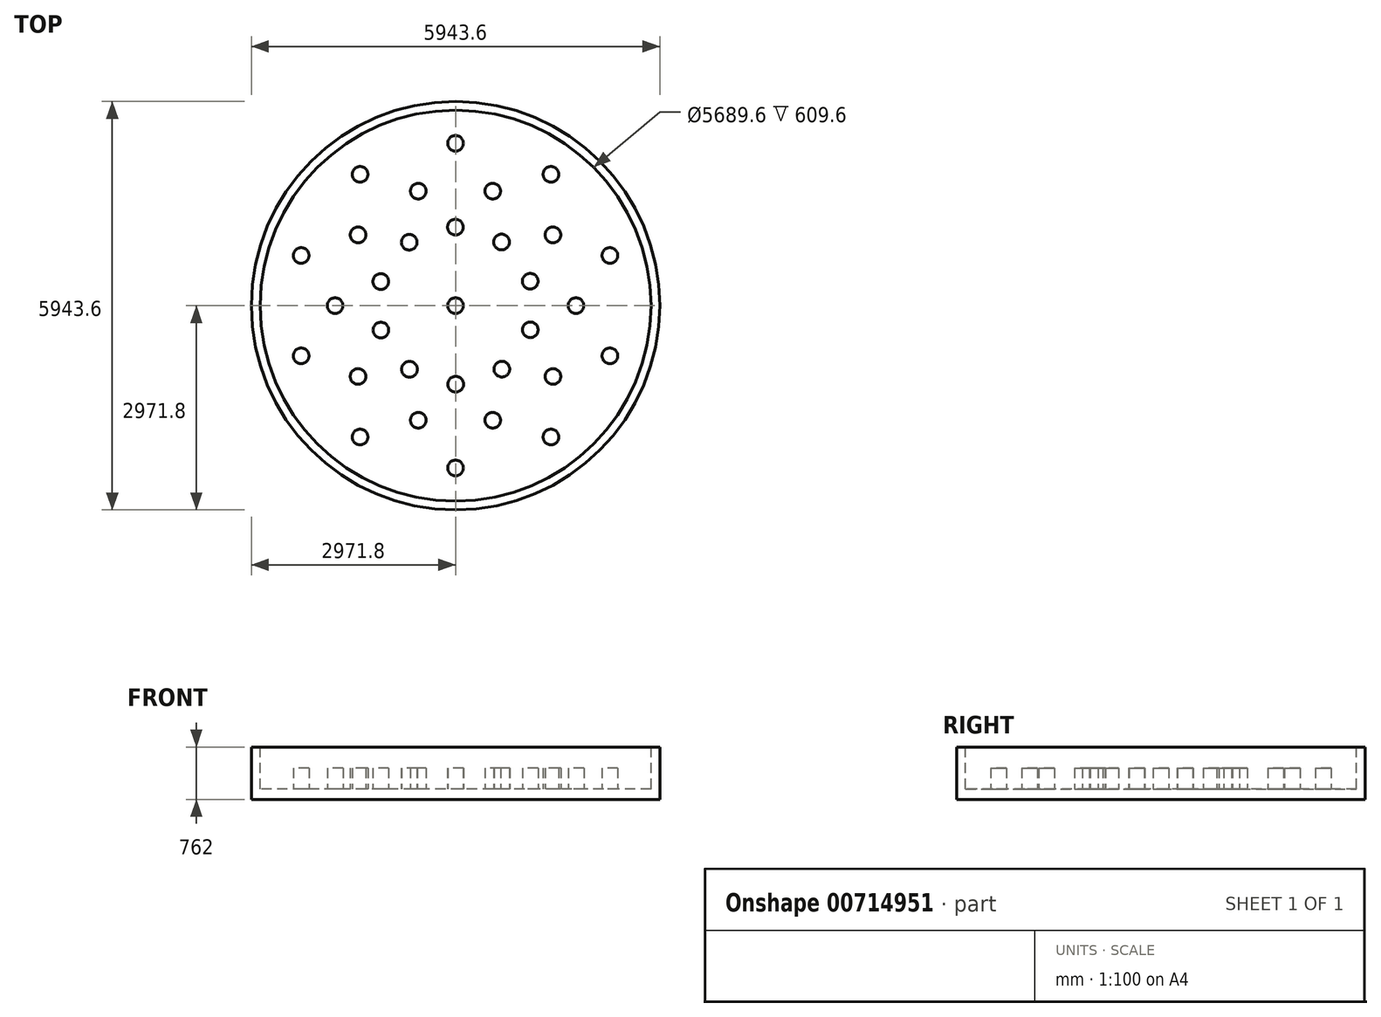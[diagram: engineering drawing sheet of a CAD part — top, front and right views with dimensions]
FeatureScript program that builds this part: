
annotation { "Feature Type Name" : "Feature", "Feature Type Description" : "" }
export const myFeature = defineFeature(function(context is Context, id is Id, definition is map)
    precondition{}
    {
        {
            var Q0;
            Q0=qCreatedBy(makeId("Top.planeOp"),FACE);
            var sketch = newSketch(context, id + "F0", { "sketchPlane" : qUnion([Q0])});
            skCircle(sketch, "E0", {"center": v(0, 0) * mm, "radius": 2971.8 * mm});
            skSolve(sketch);
        }
        {
            var Q0;
            Q0=makeQuery(id+"F0.imprint","IMPRINT",FACE,{"disambiguationData":[TD([[makeQuery(id+"F0.imprint","IMPRINT",EDGE,{"derivedFrom":sQuery(id+"F0.wireOp",EDGE,"E0")}),1.0]])]});
            extrude(context, id + "F1", {"entities" : qUnion([Q0]), "depth" : 762 * mm, "offsetDistance" : 30.48 * mm});
        }
        {
            var Q0;
            Q0=makeQuery(id+"F1.opExtrude","CAP_FACE",FACE,{"disambiguationData":[OSD([sQuery(id+"F0.wireOp",EDGE,"E0")])],"isStart":false});
            var sketch = newSketch(context, id + "F2", { "sketchPlane" : qUnion([Q0])});
            skCircle(sketch, "E1", {"center": v(0, 0) * mm, "radius": 2844.8 * mm});
            skSolve(sketch);
        }
        {
            var Q0;
            Q0=makeQuery(id+"F2.imprint","IMPRINT",FACE,{"disambiguationData":[TD([[makeQuery(id+"F2.imprint","IMPRINT",EDGE,{"derivedFrom":sQuery(id+"F2.wireOp",EDGE,"E1")}),1.0]])]});
            extrude(context, id + "F3", {"entities" : qUnion([Q0]), "operationType" : NewBodyOperationType.REMOVE, "oppositeDirection" : true, "depth" : 609.6 * mm, "offsetDistance" : 30.48 * mm});
        }
        {
            var Q0;
            Q0=makeQuery(id+"F3.boolean.opBoolean","COPY",FACE,{"derivedFrom":makeQuery(id+"F3.opExtrude","CAP_FACE",FACE,{"disambiguationData":[OSD([sQuery(id+"F2.wireOp",EDGE,"E1")])],"isStart":false})});
            var sketch = newSketch(context, id + "F4", { "sketchPlane" : qUnion([Q0])});
            skCircle(sketch, "E2", {"center": v(0, 0) * mm, "radius": 2844.8 * mm});
            skSolve(sketch);
        }
        {
            var Q0;
            Q0=makeQuery(id+"F4.imprint","IMPRINT",FACE,{"disambiguationData":[TD([[makeQuery(id+"F4.imprint","IMPRINT",EDGE,{"derivedFrom":sQuery(id+"F4.wireOp",EDGE,"E2")}),1.0]])]});
            var sketch = newSketch(context, id + "F5", { "sketchPlane" : qUnion([Q0])});
            skCircle(sketch, "E3", {"center": v(0, 0) * mm, "radius": 2362.2 * mm, "construction": true});
            skCircle(sketch, "E4", {"center": v(0, 0) * mm, "radius": 1752.6 * mm, "construction": true});
            skCircle(sketch, "E5", {"center": v(0, 2362.2) * mm, "radius": 114.3 * mm});
            skCircle(sketch, "E6", {"center": v(-1752.6, 0) * mm, "radius": 114.3 * mm});
            skCircle(sketch, "E7.1.0", {"center": v(-1388.47, 1911.06) * mm, "radius": 114.3 * mm});
            skCircle(sketch, "E7.2.0", {"center": v(-2246.59, 729.96) * mm, "radius": 114.3 * mm});
            skCircle(sketch, "E7.3.0", {"center": v(-2246.59, -729.96) * mm, "radius": 114.3 * mm});
            skCircle(sketch, "E7.4.0", {"center": v(-1388.47, -1911.06) * mm, "radius": 114.3 * mm});
            skCircle(sketch, "E7.5.0", {"center": v(0, -2362.2) * mm, "radius": 114.3 * mm});
            skCircle(sketch, "E7.6.0", {"center": v(1388.47, -1911.06) * mm, "radius": 114.3 * mm});
            skCircle(sketch, "E7.7.0", {"center": v(2246.59, -729.96) * mm, "radius": 114.3 * mm});
            skCircle(sketch, "E7.8.0", {"center": v(2246.59, 729.96) * mm, "radius": 114.3 * mm});
            skCircle(sketch, "E7.9.0", {"center": v(1388.47, 1911.06) * mm, "radius": 114.3 * mm});
            skCircle(sketch, "E8.1.0", {"center": v(-1417.88, -1030.15) * mm, "radius": 114.3 * mm});
            skCircle(sketch, "E8.2.0", {"center": v(-541.58, -1666.82) * mm, "radius": 114.3 * mm});
            skCircle(sketch, "E8.3.0", {"center": v(541.58, -1666.82) * mm, "radius": 114.3 * mm});
            skCircle(sketch, "E8.4.0", {"center": v(1417.88, -1030.15) * mm, "radius": 114.3 * mm});
            skCircle(sketch, "E8.5.0", {"center": v(1752.6, 0) * mm, "radius": 114.3 * mm});
            skCircle(sketch, "E8.6.0", {"center": v(1417.88, 1030.15) * mm, "radius": 114.3 * mm});
            skCircle(sketch, "E8.7.0", {"center": v(541.58, 1666.82) * mm, "radius": 114.3 * mm});
            skCircle(sketch, "E8.8.0", {"center": v(-541.58, 1666.82) * mm, "radius": 114.3 * mm});
            skCircle(sketch, "E8.9.0", {"center": v(-1417.88, 1030.15) * mm, "radius": 114.3 * mm});
            skCircle(sketch, "E9", {"center": v(0, 0) * mm, "radius": 114.3 * mm});
            skCircle(sketch, "E10", {"center": v(0, 0) * mm, "radius": 1143 * mm, "construction": true});
            skCircle(sketch, "E11", {"center": v(-673.72, 923.34) * mm, "radius": 114.3 * mm});
            skLineSegment(sketch, "E12", {"start": v(0, 0) * mm, "end": v(-1388.47, 1911.06) * mm, "construction": true});
            skLineSegment(sketch, "E13", {"start": v(0, 0) * mm, "end": v(-1143, 0) * mm, "construction": true});
            skCircle(sketch, "E14.1.0", {"center": v(-1087.77, 351) * mm, "radius": 114.3 * mm});
            skCircle(sketch, "E14.2.0", {"center": v(-1086.34, -355.42) * mm, "radius": 114.3 * mm});
            skCircle(sketch, "E14.3.0", {"center": v(-669.96, -926.07) * mm, "radius": 114.3 * mm});
            skCircle(sketch, "E14.4.0", {"center": v(2.32, -1143) * mm, "radius": 114.3 * mm});
            skCircle(sketch, "E14.5.0", {"center": v(673.72, -923.34) * mm, "radius": 114.3 * mm});
            skCircle(sketch, "E14.6.0", {"center": v(1087.77, -351) * mm, "radius": 114.3 * mm});
            skCircle(sketch, "E14.7.0", {"center": v(1086.34, 355.42) * mm, "radius": 114.3 * mm});
            skCircle(sketch, "E14.8.0", {"center": v(669.96, 926.07) * mm, "radius": 114.3 * mm});
            skCircle(sketch, "E14.9.0", {"center": v(-2.32, 1143) * mm, "radius": 114.3 * mm});
            skSolve(sketch);
        }
        {
            var Q0;
            Q0 = qSketchRegion(id + "F5", true);
            extrude(context, id + "F6", {"entities" : qUnion([Q0]), "operationType" : NewBodyOperationType.ADD, "depth" : 304.8 * mm, "offsetDistance" : 30.48 * mm});
        }
    });
